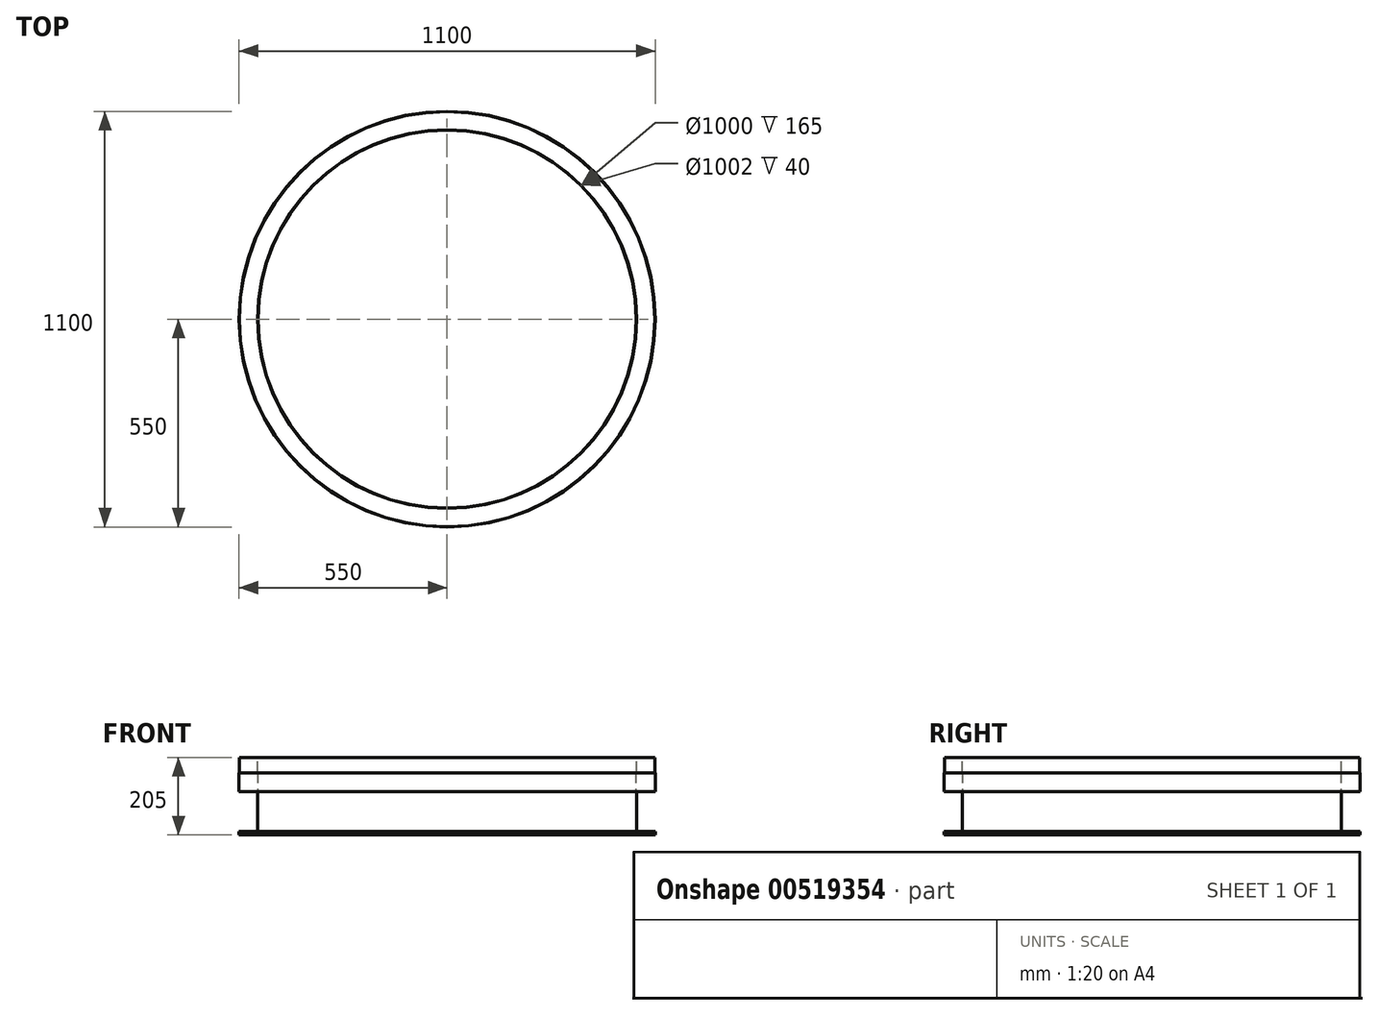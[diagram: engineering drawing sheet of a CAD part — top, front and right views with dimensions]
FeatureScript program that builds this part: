
annotation { "Feature Type Name" : "Feature", "Feature Type Description" : "" }
export const myFeature = defineFeature(function(context is Context, id is Id, definition is map)
    precondition{}
    {
        {
            var Q0;
            Q0=qCreatedBy(makeId("Front.planeOp"),FACE);
            var sketch = newSketch(context, id + "F0", { "sketchPlane" : qUnion([Q0])});
            skLineSegment(sketch, "E0", {"start": v(0, 710.75) * mm, "end": v(0, -704.58) * mm, "construction": true});
            skLineSegment(sketch, "E1", {"start": v(-500, 295.65) * mm, "end": v(-500, 410.65) * mm});
            skLineSegment(sketch, "E2", {"start": v(-500, 410.65) * mm, "end": v(-501, 410.65) * mm});
            skLineSegment(sketch, "E3", {"start": v(-549, 410.65) * mm, "end": v(-550, 410.65) * mm});
            skLineSegment(sketch, "E4", {"start": v(-550, 410.65) * mm, "end": v(-550, 360.65) * mm});
            skLineSegment(sketch, "E5", {"start": v(-550, 360.65) * mm, "end": v(-501, 360.65) * mm});
            skLineSegment(sketch, "E6", {"start": v(-501, 360.65) * mm, "end": v(-501, 295.65) * mm});
            skLineSegment(sketch, "E7", {"start": v(-549, 450.65) * mm, "end": v(-549, 410.65) * mm});
            skLineSegment(sketch, "E8", {"start": v(-549, 450.65) * mm, "end": v(-501, 450.65) * mm});
            skLineSegment(sketch, "E9", {"start": v(-501, 410.65) * mm, "end": v(-501, 450.65) * mm});
            skLineSegment(sketch, "E10", {"start": v(-500, 295.65) * mm, "end": v(-500, 255.65) * mm});
            skLineSegment(sketch, "E11", {"start": v(-501, 295.65) * mm, "end": v(-501, 255.65) * mm});
            skLineSegment(sketch, "E12", {"start": v(-501, 255.65) * mm, "end": v(-500, 255.65) * mm});
            skSolve(sketch);
        }
        {
            var Q0;
            Q0=qSketchRegion(id+"F0",true);
            var Q1;
            Q1=sQuery(id+"F0.wireOp",EDGE,"E0");
            revolve(context, id + "F1", {"entities" : qUnion([Q0]), "axis" : qUnion([Q1]), "revolveType" : RevolveType.FULL});
        }
        {
            var Q0;
            Q0=makeQuery(id+"F1.opRevolve","SWEPT_FACE",FACE,{"disambiguationData":[OSD([sQuery(id+"F0.wireOp",EDGE,"E12")])]});
            var sketch = newSketch(context, id + "F2", { "sketchPlane" : qUnion([Q0])});
            skCircle(sketch, "E13.0", {"center": v(0, 0) * mm, "radius": 500 * mm});
            skCircle(sketch, "E14", {"center": v(0, 0) * mm, "radius": 550 * mm});
            skSolve(sketch);
        }
        {
            var Q0;
            Q0 = qSketchRegion(id + "F2", true);
            extrude(context, id + "F3", {"entities" : qUnion([Q0]), "operationType" : NewBodyOperationType.ADD, "depth" : 10 * mm, "offsetDistance" : 25 * mm});
        }
    });
